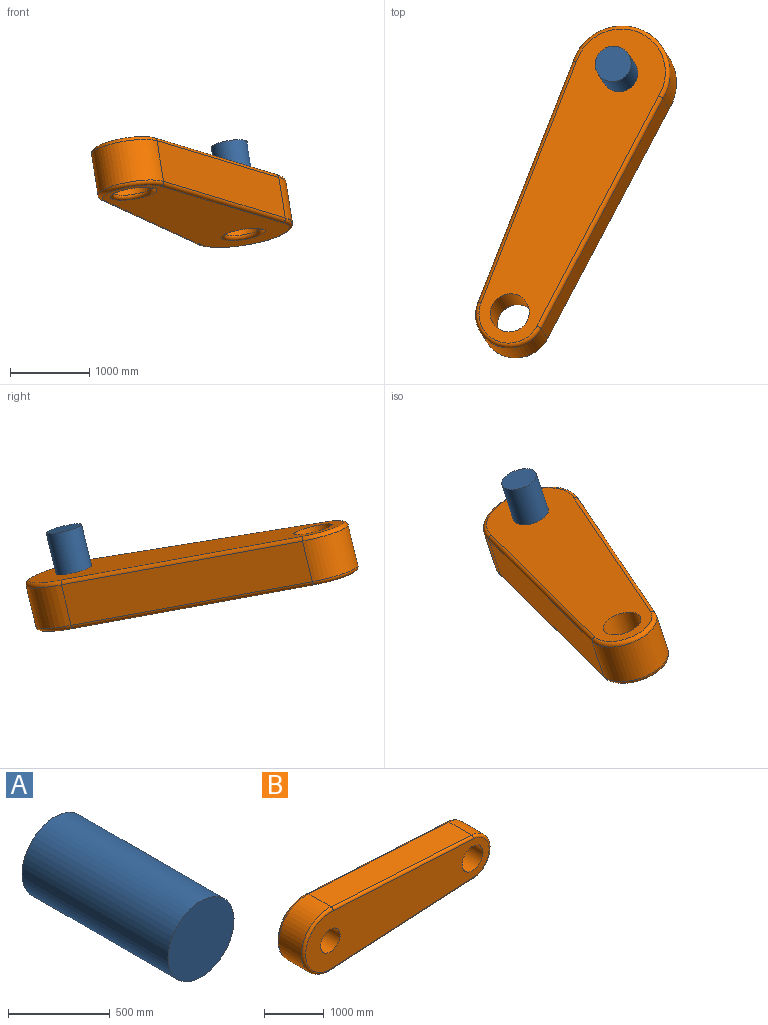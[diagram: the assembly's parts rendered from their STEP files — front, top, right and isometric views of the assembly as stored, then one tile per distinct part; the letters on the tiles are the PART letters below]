
ASSEMBLY  parts=2 mates=1
PART A: 3 faces, bbox 459.7x1016x459.7 mm
  f0: cylinder r=229.87mm len=1016mm, axis (0,1,0), area 1467424.9mm2, adj f1,f2
  f1: plane 459.74x459.74mm, normal (0,-1,0), area 166002.4mm2, adj f0
  f2: plane 459.74x459.74mm, normal (0,1,0), area 166002.4mm2, adj f0
PART B: 18 faces, bbox 4533.9x635x1374.6 mm
  f0: plane 3319.13x533.4mm, normal (0.06,0,1), area 1773239.1mm2, adj f1,f4,f8,f12
  f1: cylinder r=635mm len=1270mm, axis (0,1,0), area 1140409.4mm2, adj f0,f2,f9,f13
  f2: plane 3319.13x533.4mm, normal (0.06,0,-1), area 1773239.1mm2, adj f1,f4,f11,f15
  f3: cylinder r=231.16mm len=584.2mm, axis (0,1,0), area 848496.4mm2, adj f6,f16
  f4: cylinder r=444.5mm len=887.59mm, axis (0,1,0), area 718146.7mm2, adj f0,f2,f10,f14
  f5: cylinder r=248.85mm len=584.2mm, axis (0,1,0), area 913426.4mm2, adj f6,f17
  f6: plane 4343.4x1168.4mm, normal (0,-1,0), area 3710216.8mm2, adj f3,f5,f12,f13,f14,f15
  f7: plane 4343.4x1168.4mm, normal (0,1,0), area 3540791.5mm2, adj f8,f9,f10,f11,f16,f17
  f8: cylinder r=50.8mm len=3323.45mm, axis (-1,0,0.06), area 265318mm2, adj f0,f7,f9,f10
  f9: torus R=584.2mm, axis (0,-1,0), area 165726.9mm2, adj f1,f7,f8,f11
  f10: torus R=393.7mm, axis (0,-1,0), area 102972.8mm2, adj f4,f7,f8,f11
  f11: cylinder r=50.8mm len=3323.45mm, axis (1,0,0.06), area 265318mm2, adj f2,f7,f9,f10
  f12: cylinder r=50.8mm len=3323.45mm, axis (1,0,-0.06), area 265318mm2, adj f0,f6,f13,f14
  f13: torus R=584.2mm, axis (0,-1,0), area 165726.9mm2, adj f1,f6,f12,f15
  f14: torus R=393.7mm, axis (0,-1,0), area 102972.8mm2, adj f4,f6,f12,f15
  f15: cylinder r=50.8mm len=3323.45mm, axis (-1,0,-0.06), area 265318mm2, adj f2,f6,f13,f14
  f16: torus R=281.96mm, axis (0,-1,0), area 125152.2mm2, adj f3,f7
  f17: torus R=299.65mm, axis (0,-1,0), area 134021.1mm2, adj f5,f7
PLACE A rot(axis=(-0.58,0.46,-0.68),123.8deg) t=(-1799.65,-5411.19,628.52)mm
PLACE B rot(axis=(-0.41,0.53,-0.74),135deg) t=(-1774.7,-5449.47,471.39)mm
MATE cylindrical A.f0 <-> B.f1  axis (0.15,-0.23,-0.96) through (-1799.65,-5411.19,628.52)mm
